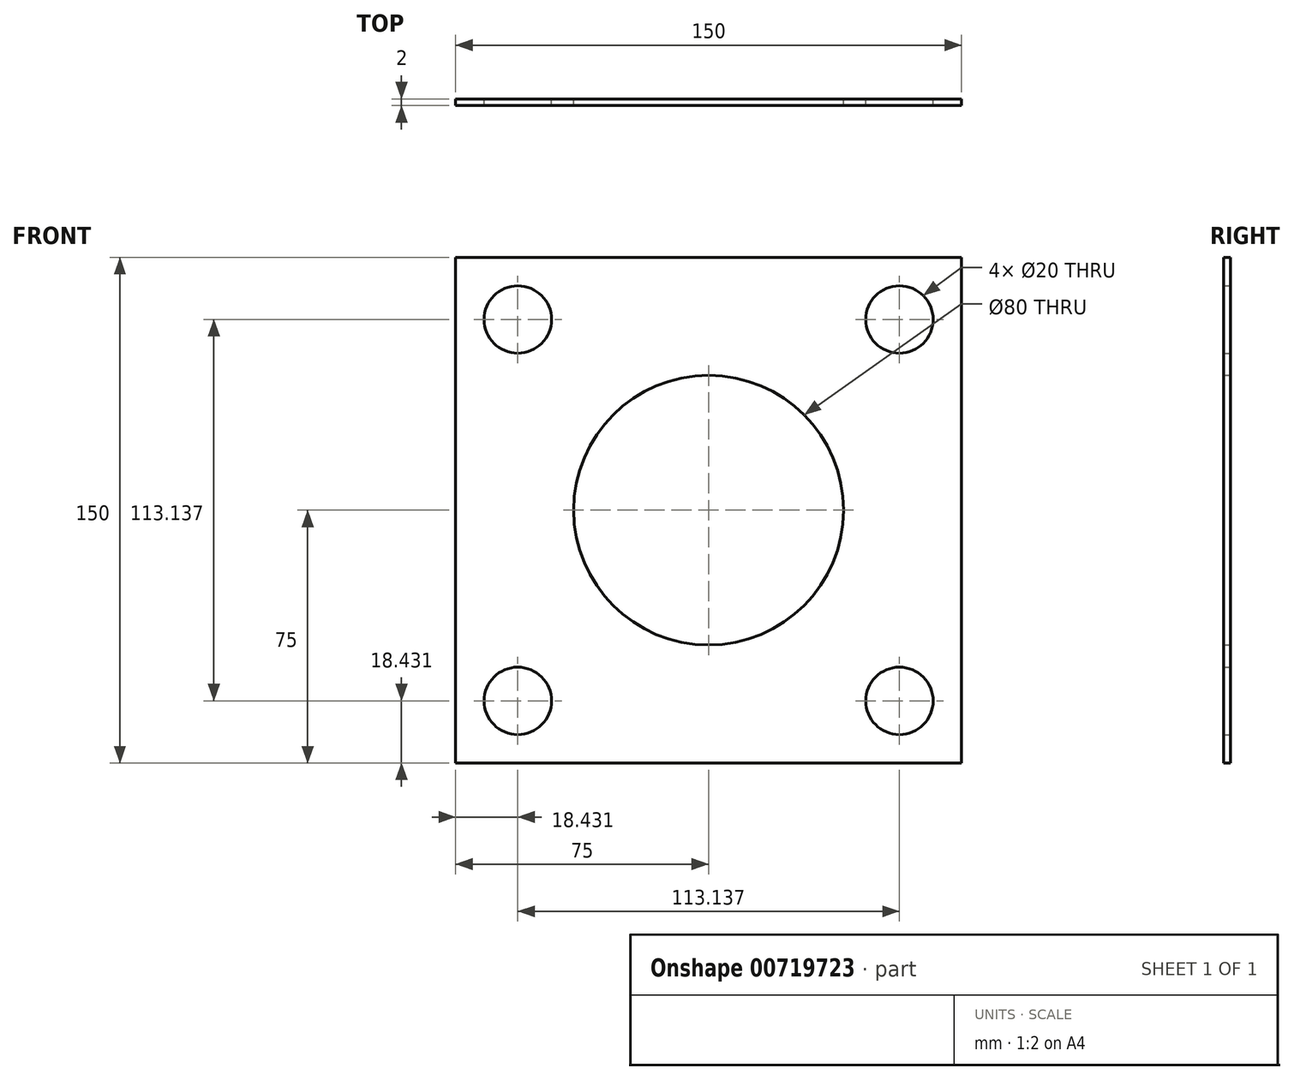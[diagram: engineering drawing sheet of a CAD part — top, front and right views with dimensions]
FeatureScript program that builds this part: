
annotation { "Feature Type Name" : "Feature", "Feature Type Description" : "" }
export const myFeature = defineFeature(function(context is Context, id is Id, definition is map)
    precondition{}
    {
        {
            var Q0;
            Q0=qCreatedBy(makeId("Front.planeOp"),FACE);
            var sketch = newSketch(context, id + "F0", { "sketchPlane" : qUnion([Q0])});
            skLineSegment(sketch, "E0.bottom", {"start": v(75, 75) * mm, "end": v(-75, 75) * mm});
            skLineSegment(sketch, "E0.top", {"start": v(75, -75) * mm, "end": v(-75, -75) * mm});
            skLineSegment(sketch, "E0.left", {"start": v(75, 75) * mm, "end": v(75, -75) * mm});
            skLineSegment(sketch, "E0.right", {"start": v(-75, 75) * mm, "end": v(-75, -75) * mm});
            skPoint(sketch, "E0.middle", {"position": v(0, 0) * mm});
            skLineSegment(sketch, "E1", {"start": v(0, 0) * mm, "end": v(56.57, 56.57) * mm});
            skLineSegment(sketch, "E2", {"start": v(0, 0) * mm, "end": v(-56.57, -56.57) * mm});
            skCircle(sketch, "E3", {"center": v(0, 0) * mm, "radius": 40 * mm});
            skCircle(sketch, "E4", {"center": v(56.57, 56.57) * mm, "radius": 10 * mm});
            skCircle(sketch, "E5", {"center": v(-56.57, -56.57) * mm, "radius": 10 * mm});
            skLineSegment(sketch, "E6", {"start": v(0, 0) * mm, "end": v(-56.57, 56.57) * mm});
            skLineSegment(sketch, "E7", {"start": v(0, 0) * mm, "end": v(56.57, -56.57) * mm});
            skCircle(sketch, "E8", {"center": v(-56.57, 56.57) * mm, "radius": 10 * mm});
            skCircle(sketch, "E9", {"center": v(56.57, -56.57) * mm, "radius": 10 * mm});
            skSolve(sketch);
        }
        {
            var Q0;
            Q0=makeQuery(id+"F0.imprint","IMPRINT",FACE,{"disambiguationData":[TD([[makeQuery(id+"F0.imprint","IMPRINT",EDGE,{"derivedFrom":sQuery(id+"F0.wireOp",EDGE,"E0.bottom")}),1.0]])]});
            extrude(context, id + "F1", {"entities" : qUnion([Q0]), "depth" : 2 * mm, "offsetDistance" : 25 * mm});
        }
    });
